# Revit family: 2059461
name_source: partatom
category: Lighting Fixtures
revit_build: Autodesk Revit 2016 (Build: 20150220_1215(x64)
units: mm (PartAtom-declared; Revit-internal decimal feet)

## family parameters
Cut with Voids When Loaded = No
Host = Face
Light Source = Yes
OmniClass Number = 23.80.70.00
OmniClass Title = Lighting
Part Type = Normal
Room Calculation Point = No
Round Connector Dimension = Use Diameter
Shared = No

## types (1)
- 2059461 ROUTELED II OPEN AREA DALI
    Apparent Load = 2 VA
    Assembly Code = D5020200
    AssetType = Fixed
    ClassificationName = Uniclass2015
    ClassificationValue = EF_70_80
    Color Filter = 16777215
    Corridor_SYL = No
    Cost = 0 $
    Default Elevation = 1219 mm
    Description = Miniature self-test (DALI) emergency recessed luminaire downlight with open area optic, non-maintained 3 hr emergency, standalone unit with inverter module and rechargeable battery (NiMH), quick and easy installation with inverter module and battery pack contained in articulated case that can pass through 40mm cutout, 219lm, 3W, IK07, beam angle 148 degrees, 230V, 50-60Hz, recharge period 24 hours, Power Factor 0.45, charge current 300mA, LxWxD (mm) 416x29x26.
    Dimming Lamp Color Temperature Shift = <None>
    DocumentationLiterature = http://www.sylvania-lighting.com
    ElectricShockClassification = Class II
    Emit Shape Visible in Rendering = No
    Emit from Circle Diameter = 16 mm  [stored 0.0524934 ft]
    IfcExportAs = IfcLightFixtureType
    IfcExportType = IfcLightFixtureType
    ImpactProtectionIndex = IK07
    IngressProtection = IP20
    Keynote = 16500
    Lamp = LED
    LampColourRenderingIndex = 70
    LampColourTemperature = 5000 K
    LampMacAdamStep = 5
    LampNominalLuminous = 219 lm
    LampsType = LED
    LightOutputRatio = 100
    LuminousEfficacy = 109.5 lm/W
    Manufacturer = Feilo Sylvania
    ManufacturerName = Feilo Sylvania
    Material = aluminium housing
    Material_1_SYL = Aluminum
    Material_2_SYL = Polycarbonate, Clear
    Material_3_SYL = LED-Sylvania
    Material_4_SYL = <By Category>
    Model = ROUTELED II OPEN AREA DALI
    ModelNumber = 2059461
    ModelReference = ROUTELED II OPEN AREA DALI
    Name = ROUTELED II OPEN AREA DALI
    NominalDepth = 27 mm
    NominalHeight = 27 mm
    NominalLength = 416 mm
    OpenArea_SYL = Yes
    Photometric Web File = 2059461.ies
    PowerConsumption = 2 W
    PowerFactor = 0
    Tilt Angle = -90.00°
    Type Image = <None>
    TypeName = ROUTELED II OPEN AREA DALI
    URL = http://www.sylvania-lighting.com
    Voltage = 0 V
    Weight = 0.948 kg

note: [stored X ft] marks values corroborated as IEEE doubles in the binary element streams (Revit-internal decimal feet)

## geometry (parser evidence)
native form markers: Sweep x3
no freeform markers — native parametric forms only
